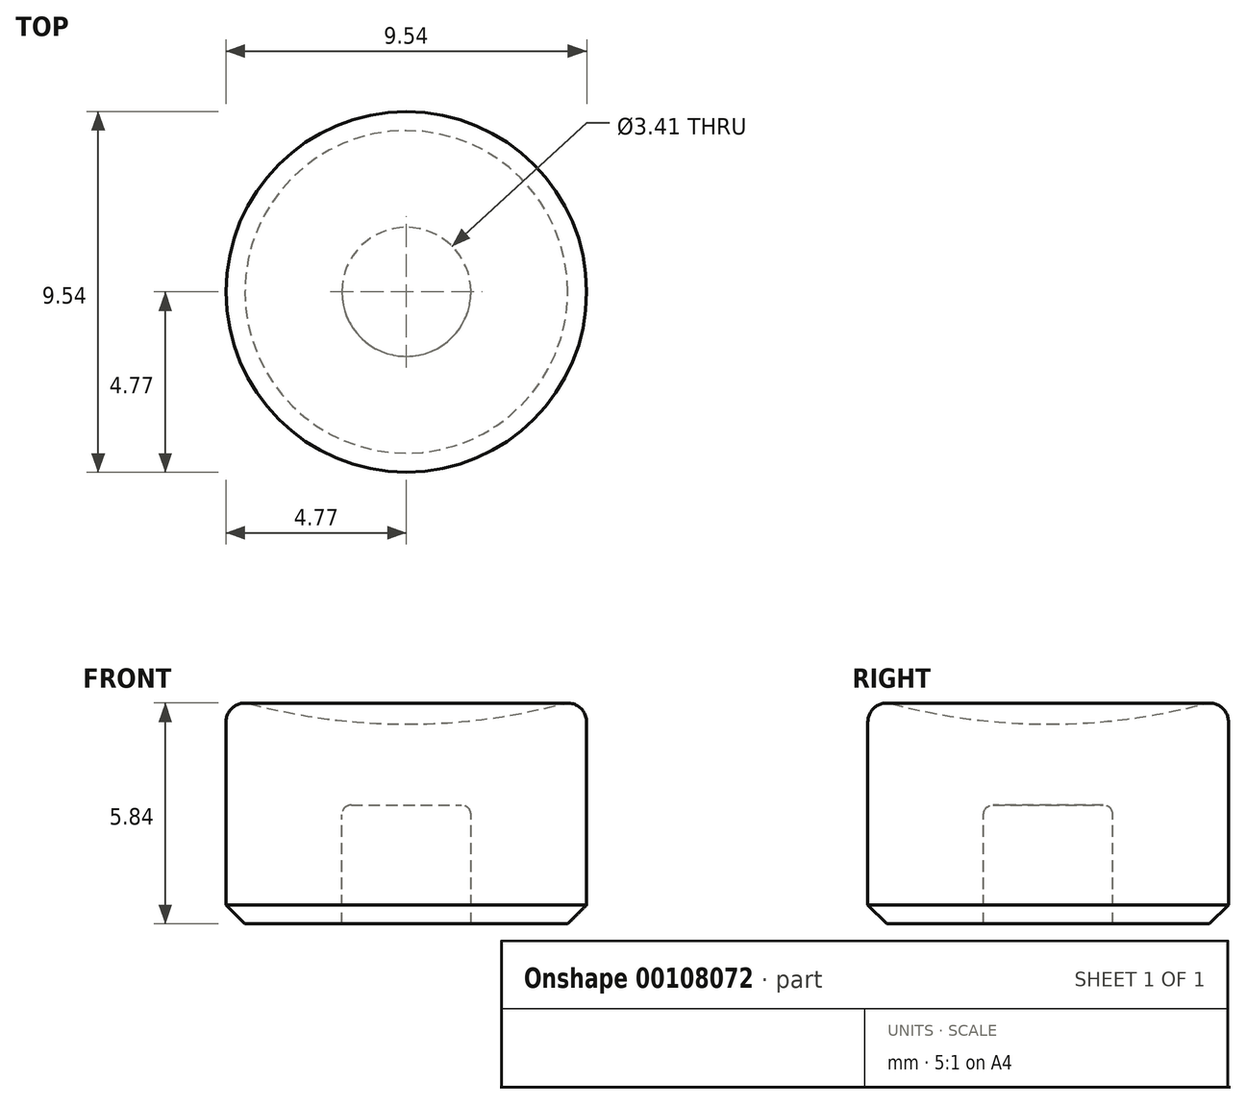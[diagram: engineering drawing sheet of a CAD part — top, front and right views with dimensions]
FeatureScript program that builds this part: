
annotation { "Feature Type Name" : "Feature", "Feature Type Description" : "" }
export const myFeature = defineFeature(function(context is Context, id is Id, definition is map)
    precondition{}
    {
        {
            var Q0;
            Q0=qCreatedBy(makeId("Front.planeOp"),FACE);
            var sketch = newSketch(context, id + "F0", { "sketchPlane" : qUnion([Q0])});
            skLineSegment(sketch, "E0", {"start": v(1.7, 0) * mm, "end": v(1.7, 3.14) * mm});
            skLineSegment(sketch, "E1", {"start": v(1.7, 0) * mm, "end": v(4.77, 0) * mm});
            skLineSegment(sketch, "E2", {"start": v(4.77, 0) * mm, "end": v(4.77, 6) * mm});
            skLineSegment(sketch, "E3", {"start": v(1.7, 3.14) * mm, "end": v(0, 3.14) * mm});
            skArc(sketch, "E4", {"start": v(0, 5.28) * mm, "mid": v(2.4, 5.46) * mm, "end": v(4.76, 6) * mm, "construction": true});
            skPoint(sketch, "E5", {"position": v(0, 5.28) * mm});
            skPoint(sketch, "E6", {"position": v(0, 6) * mm});
            skLineSegment(sketch, "E7", {"start": v(0, 5.28) * mm, "end": v(0, 3.14) * mm});
            skArc(sketch, "E8", {"start": v(0, 5.28) * mm, "mid": v(2.4, 5.46) * mm, "end": v(4.76, 6) * mm});
            skPoint(sketch, "E9.orphan", {"position": v(-4.77, 6) * mm});
            skSolve(sketch);
        }
        {
            var Q0;
            Q0=makeQuery(id+"F0.imprint","IMPRINT",FACE,{"disambiguationData":[TD([[makeQuery(id+"F0.imprint","IMPRINT",EDGE,{"derivedFrom":sQuery(id+"F0.wireOp",EDGE,"E0")}),-1.0]])]});
            var Q1;
            Q1=sQuery(id+"F0.wireOp",EDGE,"E7");
            revolve(context, id + "F1", {"entities" : qUnion([Q0]), "axis" : qUnion([Q1]), "revolveType" : RevolveType.FULL});
        }
        {
            var Q0;
            Q0=makeQuery(id+"F1.opRevolve","SWEPT_EDGE",EDGE,{"disambiguationData":[OSD([sQuery(id+"F0.wireOp",EDGE,"E1"),sQuery(id+"F0.wireOp",EDGE,"E2")])]});
            chamfer(context, id + "F2", {"entities" : qUnion([Q0]), "width" : 0.5 * mm, "tangentPropagation" : true});
        }
        {
            var Q0;
            Q0=makeQuery(id+"F1.opRevolve","SWEPT_EDGE",EDGE,{"disambiguationData":[OSD([sQuery(id+"F0.wireOp",EDGE,"E2"),sQuery(id+"F0.wireOp",EDGE,"E8")])]});
            fillet(context, id + "F3", {"entities" : qUnion([Q0]), "radius" : 0.5 * mm, "tangentPropagation" : true, "allowEdgeOverflow" : false});
        }
        {
            var Q0;
            Q0=makeQuery(id+"F1.opRevolve","SWEPT_EDGE",EDGE,{"disambiguationData":[OSD([sQuery(id+"F0.wireOp",EDGE,"E0"),sQuery(id+"F0.wireOp",EDGE,"E3")])]});
            fillet(context, id + "F4", {"entities" : qUnion([Q0]), "radius" : 0.25 * mm, "tangentPropagation" : true, "allowEdgeOverflow" : false});
        }
    });
